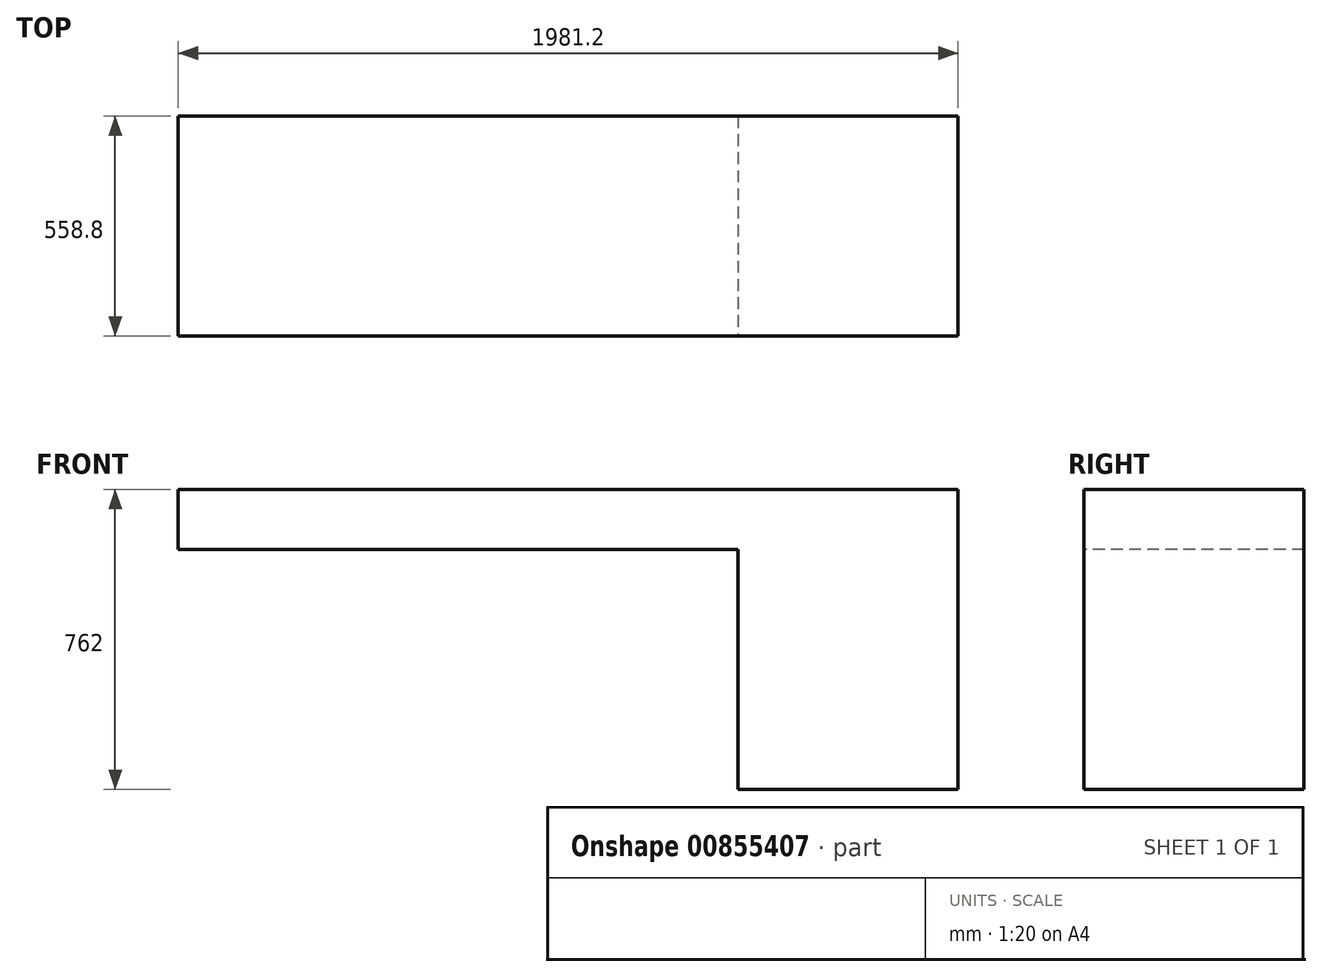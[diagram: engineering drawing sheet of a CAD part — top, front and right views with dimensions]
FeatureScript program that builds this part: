
annotation { "Feature Type Name" : "Feature", "Feature Type Description" : "" }
export const myFeature = defineFeature(function(context is Context, id is Id, definition is map)
    precondition{}
    {
        {
            var Q0;
            Q0=qCreatedBy(makeId("Top.planeOp"),FACE);
            var sketch = newSketch(context, id + "F0", { "sketchPlane" : qUnion([Q0])});
            skLineSegment(sketch, "E0.bottom", {"start": v(711.2, 279.4) * mm, "end": v(-711.2, 279.4) * mm});
            skLineSegment(sketch, "E0.top", {"start": v(711.2, -279.4) * mm, "end": v(-711.2, -279.4) * mm});
            skLineSegment(sketch, "E0.left", {"start": v(711.2, 279.4) * mm, "end": v(711.2, -279.4) * mm});
            skLineSegment(sketch, "E0.right", {"start": v(-711.2, 279.4) * mm, "end": v(-711.2, -279.4) * mm});
            skPoint(sketch, "E0.middle", {"position": v(0, 0) * mm});
            skLineSegment(sketch, "E1.bottom", {"start": v(711.2, 279.4) * mm, "end": v(1270, 279.4) * mm});
            skLineSegment(sketch, "E1.top", {"start": v(711.2, -279.4) * mm, "end": v(1270, -279.4) * mm});
            skLineSegment(sketch, "E1.right", {"start": v(1270, 279.4) * mm, "end": v(1270, -279.4) * mm});
            skSolve(sketch);
        }
        {
            var Q0;
            Q0 = qSketchRegion(id + "F0", true);
            extrude(context, id + "F1", {"entities" : qUnion([Q0]), "depth" : 762 * mm, "offsetDistance" : 25.4 * mm});
        }
        {
            var Q0;
            Q0=makeQuery(id+"F1.opExtrude","SWEPT_FACE",FACE,{"disambiguationData":[OSD([sQuery(id+"F0.wireOp",EDGE,"E0.top")])]});
            var sketch = newSketch(context, id + "F2", { "sketchPlane" : qUnion([Q0])});
            skLineSegment(sketch, "E2.bottom", {"start": v(-711.2, 762) * mm, "end": v(-711.2, 762) * mm});
            skLineSegment(sketch, "E2.top", {"start": v(-711.2, 609.6) * mm, "end": v(-711.2, 609.6) * mm});
            skLineSegment(sketch, "E2.left", {"start": v(-711.2, 762) * mm, "end": v(-711.2, 609.6) * mm});
            skLineSegment(sketch, "E2.right", {"start": v(-711.2, 762) * mm, "end": v(-711.2, 609.6) * mm});
            skLineSegment(sketch, "E3", {"start": v(-711.2, 609.6) * mm, "end": v(1270, 609.6) * mm});
            skLineSegment(sketch, "E4", {"start": v(711.2, 762) * mm, "end": v(711.2, 0) * mm});
            skSolve(sketch);
        }
        {
            var Q0;
            {var subQ0=sQuery(id+"F2.wireOp",EDGE,"E3");var subQ4=sQuery(id+"F2.wireOp",EDGE,"E4");var subQ5=makeQuery(id+"F2.imprint","INTERSECT",VERTEX,{"derivedFrom":[subQ0,subQ4]});Q0=makeQuery(id+"F2.imprint","IMPRINT",FACE,{"disambiguationData":[TD([[makeQuery(id+"F2.imprint","IMPRINT",EDGE,{"disambiguationData":[TD([[subQ5,-1.0]])],"derivedFrom":subQ4}),-1.0]])]});}
            extrude(context, id + "F3", {"entities" : qUnion([Q0]), "operationType" : NewBodyOperationType.REMOVE, "oppositeDirection" : true, "depth" : 558.8 * mm, "offsetDistance" : 25.4 * mm});
        }
    });
